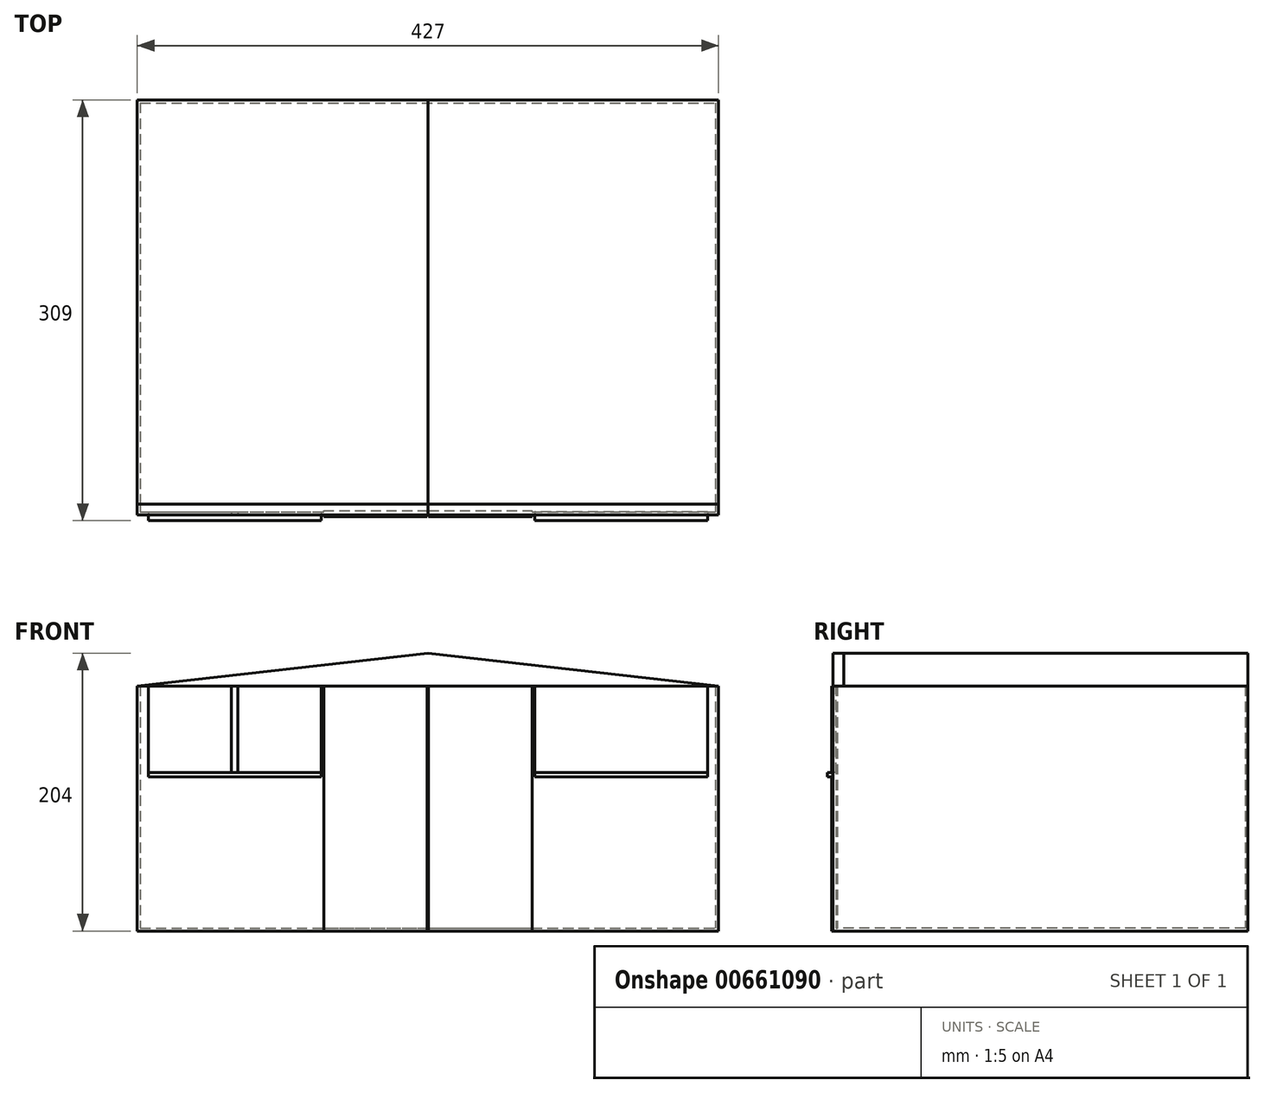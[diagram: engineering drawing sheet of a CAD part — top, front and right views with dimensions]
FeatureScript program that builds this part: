
annotation { "Feature Type Name" : "Feature", "Feature Type Description" : "" }
export const myFeature = defineFeature(function(context is Context, id is Id, definition is map)
    precondition{}
    {
        {
            var Q0;
            Q0=qCreatedBy(makeId("Top.planeOp"),FACE);
            var sketch = newSketch(context, id + "F0", { "sketchPlane" : qUnion([Q0])});
            skLineSegment(sketch, "E0.bottom", {"start": v(0, 0) * mm, "end": v(427, 0) * mm});
            skLineSegment(sketch, "E0.top", {"start": v(0, -305) * mm, "end": v(427, -305) * mm});
            skLineSegment(sketch, "E0.left", {"start": v(0, 0) * mm, "end": v(0, -305) * mm});
            skLineSegment(sketch, "E0.right", {"start": v(427, 0) * mm, "end": v(427, -305) * mm});
            skLineSegment(sketch, "E1.bottom", {"start": v(2.2, -2.2) * mm, "end": v(424.8, -2.2) * mm});
            skLineSegment(sketch, "E1.top", {"start": v(2.2, -302.8) * mm, "end": v(424.8, -302.8) * mm});
            skLineSegment(sketch, "E1.left", {"start": v(2.2, -2.2) * mm, "end": v(2.2, -302.8) * mm});
            skLineSegment(sketch, "E1.right", {"start": v(424.8, -2.2) * mm, "end": v(424.8, -302.8) * mm});
            skLineSegment(sketch, "E2.top", {"start": v(0, -365) * mm, "end": v(427, -365) * mm});
            skLineSegment(sketch, "E2.left", {"start": v(0, -305) * mm, "end": v(0, -365) * mm});
            skLineSegment(sketch, "E2.right", {"start": v(427, -305) * mm, "end": v(427, -365) * mm});
            skSolve(sketch);
        }
        {
            var Q0;
            Q0=makeQuery(id+"F0.imprint","IMPRINT",FACE,{"disambiguationData":[TD([[makeQuery(id+"F0.imprint","IMPRINT",EDGE,{"derivedFrom":sQuery(id+"F0.wireOp",EDGE,"E0.bottom")}),-1.0]])]});
            extrude(context, id + "F1", {"entities" : qUnion([Q0]), "depth" : 180 * mm, "offsetDistance" : 25 * mm});
        }
        {
            var Q0;
            Q0=makeQuery(id+"F0.imprint","IMPRINT",FACE,{"disambiguationData":[TD([[makeQuery(id+"F0.imprint","IMPRINT",EDGE,{"derivedFrom":sQuery(id+"F0.wireOp",EDGE,"E1.bottom")}),-1.0]])]});
            extrude(context, id + "F2", {"entities" : qUnion([Q0]), "operationType" : NewBodyOperationType.ADD, "depth" : 2.2 * mm, "offsetDistance" : 25 * mm});
        }
        {
            var Q0;
            Q0=makeQuery(id+"F1.opExtrude","SWEPT_FACE",FACE,{"disambiguationData":[OSD([sQuery(id+"F0.wireOp",EDGE,"E0.top")])]});
            var sketch = newSketch(context, id + "F3", { "sketchPlane" : qUnion([Q0])});
            skLineSegment(sketch, "E3.bottom", {"start": v(137, 180) * mm, "end": v(213, 180) * mm});
            skLineSegment(sketch, "E3.top", {"start": v(137, 0) * mm, "end": v(213, 0) * mm});
            skLineSegment(sketch, "E3.left", {"start": v(137, 180) * mm, "end": v(137, 0) * mm});
            skLineSegment(sketch, "E3.right", {"start": v(213, 180) * mm, "end": v(213, 0) * mm});
            skLineSegment(sketch, "E4.bottom", {"start": v(214, 180) * mm, "end": v(290, 180) * mm});
            skLineSegment(sketch, "E4.top", {"start": v(214, 0) * mm, "end": v(290, 0) * mm});
            skLineSegment(sketch, "E4.left", {"start": v(214, 180) * mm, "end": v(214, 0) * mm});
            skLineSegment(sketch, "E4.right", {"start": v(290, 180) * mm, "end": v(290, 0) * mm});
            skPoint(sketch, "E5", {"position": v(213.5, 2.2) * mm});
            skPoint(sketch, "E6", {"position": v(213, 0) * mm});
            skPoint(sketch, "E7", {"position": v(214, 0) * mm});
            skLineSegment(sketch, "E8.bottom", {"start": v(135, 180) * mm, "end": v(8, 180) * mm});
            skLineSegment(sketch, "E8.top", {"start": v(135, 116.29) * mm, "end": v(8, 116.29) * mm});
            skLineSegment(sketch, "E8.left", {"start": v(135, 180) * mm, "end": v(135, 116.29) * mm});
            skLineSegment(sketch, "E8.right", {"start": v(8, 180) * mm, "end": v(8, 116.29) * mm});
            skLineSegment(sketch, "E9.bottom", {"start": v(292, 180) * mm, "end": v(419, 180) * mm});
            skLineSegment(sketch, "E9.top", {"start": v(292, 116.29) * mm, "end": v(419, 116.29) * mm});
            skLineSegment(sketch, "E9.left", {"start": v(292, 180) * mm, "end": v(292, 116.29) * mm});
            skLineSegment(sketch, "E9.right", {"start": v(419, 180) * mm, "end": v(419, 116.29) * mm});
            skPoint(sketch, "E10", {"position": v(71.5, 180) * mm});
            skPoint(sketch, "E11", {"position": v(71.5, 116.29) * mm});
            skPoint(sketch, "E12", {"position": v(8, 148.14) * mm});
            skPoint(sketch, "E13", {"position": v(355.5, 180) * mm});
            skLineSegment(sketch, "E14.bottom", {"start": v(8, 116.29) * mm, "end": v(135, 116.29) * mm});
            skLineSegment(sketch, "E14.top", {"start": v(8, 113.29) * mm, "end": v(135, 113.29) * mm});
            skLineSegment(sketch, "E14.left", {"start": v(8, 116.29) * mm, "end": v(8, 113.29) * mm});
            skLineSegment(sketch, "E14.right", {"start": v(135, 116.29) * mm, "end": v(135, 113.29) * mm});
            skLineSegment(sketch, "E15.top", {"start": v(292, 113.29) * mm, "end": v(419, 113.29) * mm});
            skLineSegment(sketch, "E15.left", {"start": v(292, 116.29) * mm, "end": v(292, 113.29) * mm});
            skLineSegment(sketch, "E15.right", {"start": v(419, 116.29) * mm, "end": v(419, 113.29) * mm});
            skLineSegment(sketch, "E16", {"start": v(0, 180) * mm, "end": v(213.5, 204) * mm});
            skLineSegment(sketch, "E17", {"start": v(213.5, 204) * mm, "end": v(427, 180) * mm});
            skLineSegment(sketch, "E18.bottom", {"start": v(69, 180) * mm, "end": v(74, 180) * mm});
            skLineSegment(sketch, "E18.top", {"start": v(69, 116.29) * mm, "end": v(74, 116.29) * mm});
            skLineSegment(sketch, "E18.left", {"start": v(69, 180) * mm, "end": v(69, 116.29) * mm});
            skLineSegment(sketch, "E18.right", {"start": v(74, 180) * mm, "end": v(74, 116.29) * mm});
            skLineSegment(sketch, "E19.bottom", {"start": v(353, 180) * mm, "end": v(358, 180) * mm});
            skLineSegment(sketch, "E19.top", {"start": v(353, 116.29) * mm, "end": v(358, 116.29) * mm});
            skLineSegment(sketch, "E19.left", {"start": v(353, 180) * mm, "end": v(353, 116.29) * mm});
            skLineSegment(sketch, "E19.right", {"start": v(358, 180) * mm, "end": v(358, 116.29) * mm});
            skSolve(sketch);
        }
        {
            var Q0;
            Q0=makeQuery(id+"F3.imprint","IMPRINT",FACE,{"disambiguationData":[TD([[makeQuery(id+"F3.imprint","IMPRINT",EDGE,{"derivedFrom":sQuery(id+"F3.wireOp",EDGE,"E3.bottom")}),-1.0]])]});
            var Q1;
            Q1=makeQuery(id+"F3.imprint","IMPRINT",FACE,{"disambiguationData":[TD([[makeQuery(id+"F3.imprint","IMPRINT",EDGE,{"derivedFrom":sQuery(id+"F3.wireOp",EDGE,"E4.bottom")}),-1.0]])]});
            var Q2;
            Q2=makeQuery(id+"F3.imprint","IMPRINT",FACE,{"disambiguationData":[TD([[makeQuery(id+"F3.imprint","IMPRINT",EDGE,{"derivedFrom":sQuery(id+"F3.wireOp",EDGE,"E18.bottom")}),-1.0]])]});
            var Q3;
            Q3=makeQuery(id+"F3.imprint","IMPRINT",FACE,{"disambiguationData":[TD([[makeQuery(id+"F3.imprint","IMPRINT",EDGE,{"derivedFrom":sQuery(id+"F3.wireOp",EDGE,"E19.bottom")}),-1.0]])]});
            extrude(context, id + "F4", {"entities" : qUnion([Q0, Q1, Q2, Q3]), "operationType" : NewBodyOperationType.ADD, "depth" : 1 * mm, "offsetDistance" : 25 * mm, "hasSecondDirection" : true, "secondDirectionOppositeDirection" : true, "secondDirectionDepth" : 3.3 * mm});
        }
        {
            var Q0;
            Q0=makeQuery(id+"F3.imprint","IMPRINT",FACE,{"disambiguationData":[TD([[makeQuery(id+"F3.imprint","IMPRINT",EDGE,{"derivedFrom":sQuery(id+"F3.wireOp",EDGE,"E8.bottom")}),1.0]])]});
            var Q1;
            Q1=makeQuery(id+"F3.imprint","IMPRINT",FACE,{"disambiguationData":[TD([[makeQuery(id+"F3.imprint","IMPRINT",EDGE,{"derivedFrom":sQuery(id+"F3.wireOp",EDGE,"E9.bottom")}),-1.0]])]});
            var Q2;
            {var subQ0=sQuery(id+"F3.wireOp",EDGE,"E9.left");var subQ1=sQuery(id+"F3.wireOp",EDGE,"E9.top");var subQ2=makeQuery(id+"F3.imprint","INTERSECT",VERTEX,{"derivedFrom":[subQ1,subQ0]});Q2=makeQuery(id+"F3.imprint","IMPRINT",FACE,{"disambiguationData":[TD([[makeQuery(id+"F3.imprint","IMPRINT",EDGE,{"disambiguationData":[TD([[subQ2,-1.0]])],"derivedFrom":subQ1}),1.0]])]});}
            var Q3;
            {var subQ7=sQuery(id+"F3.wireOp",EDGE,"YfnkvgQr-QRok-V14t-g57v-lyYDbdyxjaZ6.top");Q3=makeQuery(id+"F3.imprint","IMPRINT",FACE,{"disambiguationData":[TD([[makeQuery(id+"F3.imprint","IMPRINT",EDGE,{"derivedFrom":subQ7}),1.0]])]});}
            var Q4;
            {var subQ0=sQuery(id+"F3.wireOp",EDGE,"YfnkvgQr-QRok-V14t-g57v-lyYDbdyxjaZ6.bottom");Q4=makeQuery(id+"F3.imprint","IMPRINT",FACE,{"disambiguationData":[TD([[makeQuery(id+"F3.imprint","IMPRINT",EDGE,{"derivedFrom":subQ0}),-1.0]])]});}
            var Q5;
            {var subQ0=sQuery(id+"F3.wireOp",EDGE,"E8.left");var subQ1=sQuery(id+"F3.wireOp",EDGE,"E8.top");var subQ2=makeQuery(id+"F3.imprint","INTERSECT",VERTEX,{"derivedFrom":[subQ1,subQ0]});Q5=makeQuery(id+"F3.imprint","IMPRINT",FACE,{"disambiguationData":[TD([[makeQuery(id+"F3.imprint","IMPRINT",EDGE,{"disambiguationData":[TD([[subQ2,-1.0]])],"derivedFrom":subQ1}),-1.0]])]});}
            var Q6;
            {var subQ0=sQuery(id+"F3.wireOp",EDGE,"E8.right");var subQ1=sQuery(id+"F3.wireOp",EDGE,"E8.top");var subQ2=makeQuery(id+"F3.imprint","INTERSECT",VERTEX,{"derivedFrom":[subQ1,subQ0]});Q6=makeQuery(id+"F3.imprint","IMPRINT",FACE,{"disambiguationData":[TD([[makeQuery(id+"F3.imprint","IMPRINT",EDGE,{"disambiguationData":[TD([[subQ2,1.0]])],"derivedFrom":subQ1}),-1.0]])]});}
            var Q7;
            {var subQ0=sQuery(id+"F3.wireOp",EDGE,"E14.bottom");var subQ5=sQuery(id+"F3.wireOp",EDGE,"sOry4WVp-PIxf-8NyE-KQ36-WmRoLQExKCCO.left");var subQ6=makeQuery(id+"F3.imprint","INTERSECT",VERTEX,{"derivedFrom":[subQ5,subQ0]});Q7=makeQuery(id+"F3.imprint","IMPRINT",FACE,{"disambiguationData":[TD([[makeQuery(id+"F3.imprint","IMPRINT",EDGE,{"disambiguationData":[TD([[subQ6,1.0]])],"derivedFrom":subQ5}),-1.0]])]});}
            var Q8;
            {var subQ0=sQuery(id+"F3.wireOp",EDGE,"E14.bottom");var subQ5=sQuery(id+"F3.wireOp",EDGE,"sOry4WVp-PIxf-8NyE-KQ36-WmRoLQExKCCO.right");var subQ6=makeQuery(id+"F3.imprint","INTERSECT",VERTEX,{"derivedFrom":[subQ5,subQ0]});Q8=makeQuery(id+"F3.imprint","IMPRINT",FACE,{"disambiguationData":[TD([[makeQuery(id+"F3.imprint","IMPRINT",EDGE,{"disambiguationData":[TD([[subQ6,1.0]])],"derivedFrom":subQ5}),1.0]])]});}
            var Q9;
            {var subQ0=sQuery(id+"F3.wireOp",EDGE,"E9.top");var subQ5=sQuery(id+"F3.wireOp",EDGE,"OYBSw6cz-BSUv-Zrt5-bxVA-wndxCvquLag2.left");var subQ7=makeQuery(id+"F3.imprint","INTERSECT",VERTEX,{"derivedFrom":[subQ5,subQ0]});Q9=makeQuery(id+"F3.imprint","IMPRINT",FACE,{"disambiguationData":[TD([[makeQuery(id+"F3.imprint","IMPRINT",EDGE,{"disambiguationData":[TD([[subQ7,1.0]])],"derivedFrom":subQ5}),-1.0]])]});}
            var Q10;
            {var subQ0=sQuery(id+"F3.wireOp",EDGE,"E9.top");var subQ3=makeQuery(id+"F3.imprint","IMPRINT",VERTEX,{"disambiguationData":[OD(1.0)],"derivedFrom":subQ0});Q10=makeQuery(id+"F3.imprint","IMPRINT",FACE,{"disambiguationData":[TD([[makeQuery(id+"F3.imprint","IMPRINT",EDGE,{"disambiguationData":[TD([[subQ3,1.0]])],"derivedFrom":subQ0}),1.0]])]});}
            extrude(context, id + "F5", {"entities" : qUnion([Q0, Q1, Q2, Q3, Q4, Q5, Q6, Q7, Q8, Q9, Q10]), "operationType" : NewBodyOperationType.REMOVE, "oppositeDirection" : true, "depth" : 25 * mm, "offsetDistance" : 25 * mm});
        }
        {
            var Q0;
            {var subQ10=sQuery(id+"F3.wireOp",EDGE,"E3.bottom");Q0=makeQuery(id+"F3.imprint","IMPRINT",FACE,{"disambiguationData":[TD([[makeQuery(id+"F3.imprint","IMPRINT",EDGE,{"derivedFrom":subQ10}),1.0]])]});}
            extrude(context, id + "F6", {"entities" : qUnion([Q0]), "operationType" : NewBodyOperationType.ADD, "oppositeDirection" : true, "depth" : 8 * mm, "offsetDistance" : 25 * mm});
        }
        {
            var Q0;
            Q0=makeQuery(id+"F3.imprint","IMPRINT",FACE,{"disambiguationData":[TD([[makeQuery(id+"F3.imprint","IMPRINT",EDGE,{"derivedFrom":sQuery(id+"F3.wireOp",EDGE,"E15.top")}),1.0]])]});
            var Q1;
            Q1=makeQuery(id+"F3.imprint","IMPRINT",FACE,{"disambiguationData":[TD([[makeQuery(id+"F3.imprint","IMPRINT",EDGE,{"derivedFrom":sQuery(id+"F3.wireOp",EDGE,"E14.top")}),1.0]])]});
            extrude(context, id + "F7", {"entities" : qUnion([Q0, Q1]), "operationType" : NewBodyOperationType.ADD, "depth" : 4 * mm, "offsetDistance" : 25 * mm});
        }
        {
            var Q0;
            Q0=makeQuery(id+"F1.opExtrude","SWEPT_FACE",FACE,{"disambiguationData":[OSD([sQuery(id+"F0.wireOp",EDGE,"E0.bottom")])]});
            var sketch = newSketch(context, id + "F8", { "sketchPlane" : qUnion([Q0])});
            skLineSegment(sketch, "E20", {"start": v(-427, 180) * mm, "end": v(-213.5, 204) * mm});
            skPoint(sketch, "E20.endSnap0", {"position": v(-213.5, 180) * mm});
            skLineSegment(sketch, "E21", {"start": v(-213.5, 204) * mm, "end": v(0, 180) * mm});
            skSolve(sketch);
        }
        {
            var Q0;
            Q0=makeQuery(id+"F8.imprint","IMPRINT",FACE,{"disambiguationData":[TD([[makeQuery(id+"F8.imprint","IMPRINT",EDGE,{"derivedFrom":sQuery(id+"F8.wireOp",EDGE,"E20")}),-1.0]])]});
            extrude(context, id + "F9", {"entities" : qUnion([Q0]), "oppositeDirection" : true, "depth" : 305 * mm, "offsetDistance" : 25 * mm});
        }
        {
            var Q0;
            Q0=makeQuery(id+"F4.opExtrude","CAP_FACE",FACE,{"disambiguationData":[OSD([sQuery(id+"F3.wireOp",EDGE,"E3.bottom"),sQuery(id+"F3.wireOp",EDGE,"E3.top"),sQuery(id+"F3.wireOp",EDGE,"E3.left"),sQuery(id+"F3.wireOp",EDGE,"E3.right")])],"isStart":false});
            var sketch = newSketch(context, id + "F10", { "sketchPlane" : qUnion([Q0])});
            skText(sketch, "E22", { "text": "10*14", "fontName": "OpenSans-Bold.ttf"});
            const initialGuessF10  = {"E22": [0.1187, 0.12722, 1, 0, 0.03968]};
            skSetInitialGuess(sketch, initialGuessF10);
            skSolve(sketch);
        }
        {
            var Q0;
            Q0 = qConstructionFilter(qBodyType(qCreatedBy(id + "F10" ,EDGE), BodyType.WIRE), ConstructionObject.NO);
            extrude(context, id + "F11", {"bodyType" : ToolBodyType.SURFACE, "surfaceEntities" : qUnion([Q0]), "depth" : 10 * mm, "offsetDistance" : 25 * mm});
        }
    });
